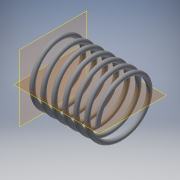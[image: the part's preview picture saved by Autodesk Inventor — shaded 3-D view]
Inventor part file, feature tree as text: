
AUTODESK INVENTOR PART (.ipt)
format: ipt  version: 2016 (Build 200138000, 138)  size: 427,008 bytes
history: native  units: in
note: dims shown in document units (in); Inventor stores cm internally (conversion verified against a paired STEP export)
features: sketch x4, extrude x2, helix x2, plane x1
ambient origin geometry x8: Origin, YZ Plane, XZ Plane, XY Plane, X Axis, Y Axis, Z Axis, Center Point
bodies: Body1 (feature_tree)
feature tree (9):
  extrude  "Extrusion6"  Depth=0.1575in
  helix  "Coil5"  [1 undecoded]
  helix  "Coil6"  [1 undecoded]
  plane  "Work Plane2"
  extrude  "Extrusion7"  Depth=1.0787in
  sketch  "Sketch10"  dims[d62=0.0in d65=0.1575in d66=0.7874in]
  sketch  "Sketch11"  dims[d67=1.5748in d68=0.0in d69=90.0deg d70=90.0deg d71=0.0in d72=0.0in d73=0.0472in d74=0.315in]
  sketch  "Sketch12"  dims[d75=0.0591in d76=0.315in]
  sketch  "Sketch13"  dims[d77=1.5748in d78=0.0in d79=90.0deg d80=90.0deg d81=0.0in d82=0.0in d83=1.0787in d84=0.0787in d85=0.0in]
note: 2 required parameter values undecoded (feature->parameter linkage not recoverable at this tier; creation-order binding heuristic only, values carry confidence <= 0.55)
